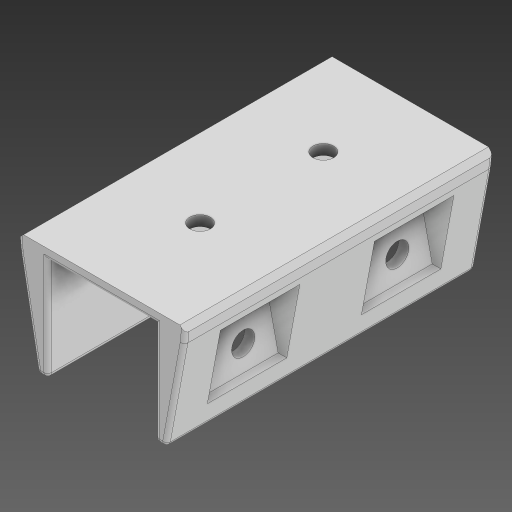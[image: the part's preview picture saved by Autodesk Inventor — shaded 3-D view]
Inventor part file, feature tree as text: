
AUTODESK INVENTOR PART (.ipt)
format: ipt  version: 2024 (Build 280153000, 153)  size: 385,536 bytes
history: native  units: mm
features: sketch x5, chamfer x4, extrude x3, plane x3, hole x2, fillet x2, mirror x2, projected_geometry x2
ambient origin geometry x8: Origin, YZ Plane, XZ Plane, XY Plane, X Axis, Y Axis, Z Axis, Center Point
bodies: Body1 (feature_tree)
feature tree (23):
  extrude  "Extrusion2"  Depth=60.07774mm
  hole  "Hole1"  [1 undecoded]
  extrude  "Extrusion3"  Depth=2.0mm
  fillet  "Fillet1"  Radius=2.0mm
  plane  "Work Plane3"
  extrude  "Extrusion4"  Depth=2.0mm
  hole  "Hole2"  [1 undecoded]
  plane  "Work Plane4"
  mirror  "Mirror2"
  mirror  "Mirror3"
  chamfer  "Chamfer1"  Distance=2.0mm
  chamfer  "Chamfer2"  Distance=0.75mm
  chamfer  "Chamfer3"  Distance=15.0mm
  chamfer  "Chamfer4"  Distance=2.0mm
  fillet  "Fillet3"  Radius=10.0mm
  sketch  "Sketch1"  dims[d27=24.0mm d28=60.07774mm]
  sketch  "Sketch2"  dims[d29=32.44mm d30=19.14674mm]
  sketch  "Sketch3"  dims[d31=16.22mm d32=3.458734mm d33=2.0mm d34=0.0mm]
  plane  "Work Plane2"
  sketch  "Sketch4"  dims[d35=4.0mm d36=6.0mm d37=4.0mm d38=2.0mm d39=90.0deg d40=8.0mm d41=20.594885mm d42=10.5mm]
  sketch  "Sketch5"  dims[d43=2.0mm d44=20.0mm d45=2.0mm d46=0.0mm d47=0.75mm d50=15.0mm d51=2.0mm d52=10.0mm d53=5.0mm d54=10.0mm d55=0.0mm d56=4.5mm d57=6.0mm d58=8.0mm d59=4.0mm d60=90.0deg d61=8.0mm d62=20.594885mm d63=5.0mm d64=5.0mm d65=2.73mm d66=2.0mm d67=45.0deg d68=2.79mm d69=2.0mm d70=45.0deg d71=0.93mm d72=2.0mm d73=45.0deg d74=1.0mm d75=2.0mm d76=45.0deg d77=0.75mm d48=0.0mm d49=0.0mm]
  projected_geometry  "Project Cut Edges1"
  projected_geometry  "Project Cut Edges2"
note: 2 required parameter values undecoded (feature->parameter linkage not recoverable at this tier; creation-order binding heuristic only, values carry confidence <= 0.55)
